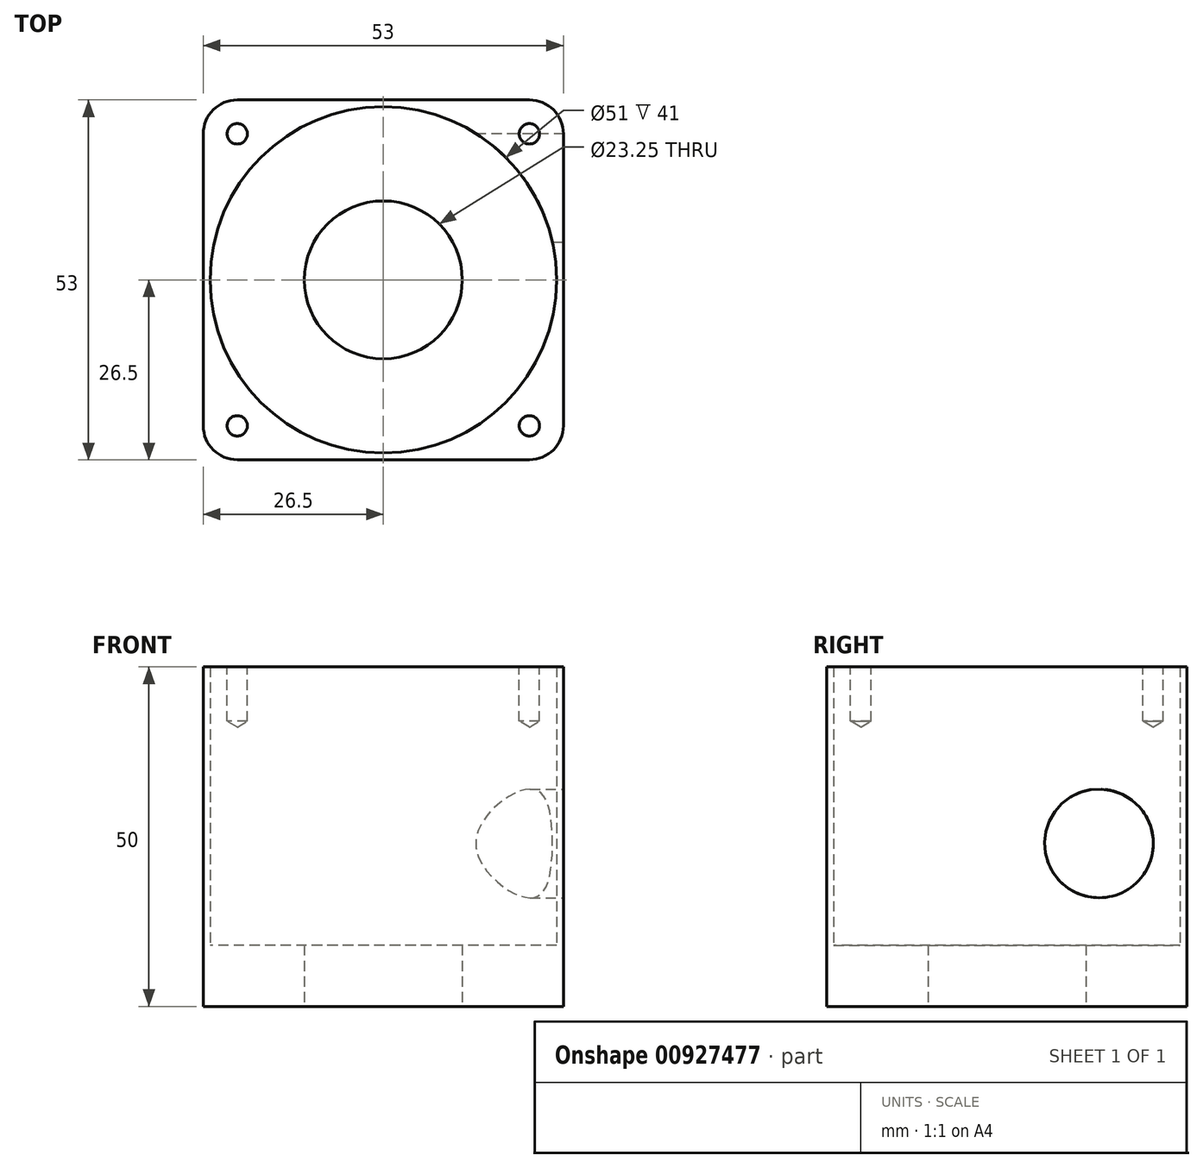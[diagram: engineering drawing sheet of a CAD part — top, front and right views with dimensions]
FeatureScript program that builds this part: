
annotation { "Feature Type Name" : "Feature", "Feature Type Description" : "" }
export const myFeature = defineFeature(function(context is Context, id is Id, definition is map)
    precondition{}
    {
        {
            var Q0;
            Q0=qCreatedBy(makeId("Top.planeOp"),FACE);
            var sketch = newSketch(context, id + "F0", { "sketchPlane" : qUnion([Q0])});
            skLineSegment(sketch, "E0.bottom", {"start": v(-21.5, 26.5) * mm, "end": v(21.5, 26.5) * mm});
            skLineSegment(sketch, "E0.top", {"start": v(-21.5, -26.5) * mm, "end": v(21.5, -26.5) * mm});
            skLineSegment(sketch, "E0.left", {"start": v(-26.5, 21.5) * mm, "end": v(-26.5, -21.5) * mm});
            skLineSegment(sketch, "E0.right", {"start": v(26.5, 21.5) * mm, "end": v(26.5, -21.5) * mm});
            skPoint(sketch, "E0.middle", {"position": v(0, 0) * mm});
            skCircle(sketch, "E1", {"center": v(0, 0) * mm, "radius": 25.5 * mm});
            skCircle(sketch, "E2", {"center": v(0, 0) * mm, "radius": 11.62 * mm});
            skPoint(sketch, "E3.visualSharp", {"position": v(-26.5, 26.5) * mm});
            skArc(sketch, "E3.filletArc", {"start": v(-21.5, 26.5) * mm, "mid": v(-25.04, 25.04) * mm, "end": v(-26.5, 21.5) * mm});
            skPoint(sketch, "E4.visualSharp", {"position": v(26.5, 26.5) * mm});
            skArc(sketch, "E4.filletArc", {"start": v(26.5, 21.5) * mm, "mid": v(25.04, 25.04) * mm, "end": v(21.5, 26.5) * mm});
            skPoint(sketch, "E5.visualSharp", {"position": v(26.5, -26.5) * mm});
            skArc(sketch, "E5.filletArc", {"start": v(21.5, -26.5) * mm, "mid": v(25.04, -25.04) * mm, "end": v(26.5, -21.5) * mm});
            skPoint(sketch, "E6.visualSharp", {"position": v(-26.5, -26.5) * mm});
            skArc(sketch, "E6.filletArc", {"start": v(-26.5, -21.5) * mm, "mid": v(-25.04, -25.04) * mm, "end": v(-21.5, -26.5) * mm});
            skSolve(sketch);
        }
        {
            var Q0;
            Q0 = qSketchRegion(id + "F0", true);
            extrude(context, id + "F1", {"entities" : qUnion([Q0]), "depth" : 50 * mm, "offsetDistance" : 25 * mm});
        }
        {
            var Q0;
            Q0=makeQuery(id+"F0.imprint","IMPRINT",FACE,{"disambiguationData":[TD([[makeQuery(id+"F0.imprint","IMPRINT",EDGE,{"derivedFrom":sQuery(id+"F0.wireOp",EDGE,"E1")}),1.0]])]});
            extrude(context, id + "F2", {"entities" : qUnion([Q0]), "operationType" : NewBodyOperationType.ADD, "depth" : 9 * mm, "offsetDistance" : 25 * mm});
        }
        {
            var Q0;
            Q0=qCreatedBy(makeId("Right.planeOp"),FACE);
            cPlane(context, id + "F3", {"entities" : qUnion([Q0]), "cplaneType" : CPlaneType.OFFSET, "offset" : 26.5 * mm, "width" : 150 * mm, "height" : 150 * mm});
        }
        {
            var Q0;
            Q0=qCreatedBy(id+"F3.planeOp",FACE);
            var sketch = newSketch(context, id + "F4", { "sketchPlane" : qUnion([Q0])});
            skPoint(sketch, "E7", {"position": v(13.56, 24) * mm});
            skCircle(sketch, "E8", {"center": v(13.56, 24) * mm, "radius": 8 * mm});
            skSolve(sketch);
        }
        {
            var Q0;
            Q0 = qSketchRegion(id + "F4", true);
            extrude(context, id + "F5", {"entities" : qUnion([Q0]), "operationType" : NewBodyOperationType.REMOVE, "oppositeDirection" : true, "depth" : 15 * mm, "offsetDistance" : 25 * mm});
        }
        {
            var Q0;
            Q0=qCreatedBy(makeId("Top.planeOp"),FACE);
            cPlane(context, id + "F6", {"entities" : qUnion([Q0]), "cplaneType" : CPlaneType.OFFSET, "offset" : 50 * mm, "width" : 150 * mm, "height" : 150 * mm});
        }
        {
            var Q0;
            Q0=qCreatedBy(id+"F6.planeOp",FACE);
            var sketch = newSketch(context, id + "F7", { "sketchPlane" : qUnion([Q0])});
            skPoint(sketch, "E9", {"position": v(-21.5, 21.5) * mm});
            skPoint(sketch, "E10", {"position": v(21.5, 21.5) * mm});
            skPoint(sketch, "E11", {"position": v(21.5, -21.5) * mm});
            skPoint(sketch, "E12", {"position": v(-21.5, -21.5) * mm});
            skSolve(sketch);
        }
        {
            var Q0;
            Q0=sQuery(id+"F7.wireOp",VERTEX,"E9");
            var Q1;
            Q1=sQuery(id+"F7.wireOp",VERTEX,"E10");
            var Q2;
            Q2=sQuery(id+"F7.wireOp",VERTEX,"E11");
            var Q3;
            Q3=sQuery(id+"F7.wireOp",VERTEX,"E12");
            var Q4;
            Q4=makeQuery(id+"F1.opExtrude","SWEPT_BODY",BODY,{"disambiguationData":[OSD([sQuery(id+"F0.wireOp",EDGE,"E0.bottom"),sQuery(id+"F0.wireOp",EDGE,"E0.top"),sQuery(id+"F0.wireOp",EDGE,"E0.left"),sQuery(id+"F0.wireOp",EDGE,"E0.right"),sQuery(id+"F0.wireOp",EDGE,"E1"),sQuery(id+"F0.wireOp",EDGE,"E3.filletArc"),sQuery(id+"F0.wireOp",EDGE,"E4.filletArc"),sQuery(id+"F0.wireOp",EDGE,"E5.filletArc"),sQuery(id+"F0.wireOp",EDGE,"E6.filletArc")])]});
            hole(context, id + "F8", {"style" : HoleStyle.SIMPLE, "endStyle" : HoleEndStyle.BLIND, "holeDiameter" : 3 * mm, "majorDiameter" : 5 * mm, "holeDepth" : 8 * mm, "isTappedThrough" : true, "tappedDepth" : 12 * mm, "tapClearance" : 3, "startFromSketch" : true, "locations" : qUnion([Q0, Q1, Q2, Q3]), "scope" : qUnion([Q4])});
        }
    });
